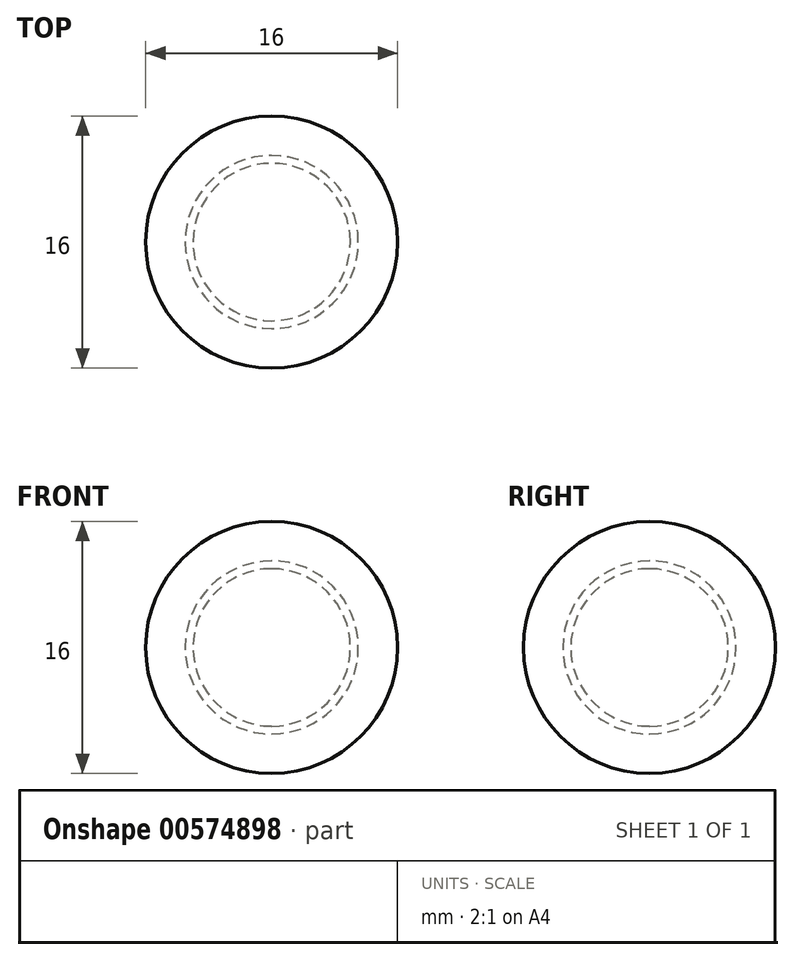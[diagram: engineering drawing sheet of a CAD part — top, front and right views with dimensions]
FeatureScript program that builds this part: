
annotation { "Feature Type Name" : "Feature", "Feature Type Description" : "" }
export const myFeature = defineFeature(function(context is Context, id is Id, definition is map)
    precondition{}
    {
        {
            var Q0;
            Q0=qCreatedBy(makeId("Right.planeOp"),FACE);
            var sketch = newSketch(context, id + "F0", { "sketchPlane" : qUnion([Q0])});
            skLineSegment(sketch, "E0", {"start": v(0, -5) * mm, "end": v(0, 5) * mm});
            skArc(sketch, "E1", {"start": v(0, -5) * mm, "mid": v(5, 0) * mm, "end": v(0, 5) * mm});
            skArc(sketch, "E2.0", {"start": v(0, -8) * mm, "mid": v(8, 0) * mm, "end": v(0, 8) * mm});
            skLineSegment(sketch, "E3", {"start": v(0, 5) * mm, "end": v(0, 8) * mm});
            skLineSegment(sketch, "E4", {"start": v(0, -5) * mm, "end": v(0, -8) * mm});
            skArc(sketch, "E5.0", {"start": v(0, -5.5) * mm, "mid": v(5.5, 0) * mm, "end": v(0, 5.5) * mm});
            skSolve(sketch);
        }
        {
            var Q0;
            Q0=makeQuery(id+"F0.imprint","IMPRINT",FACE,{"disambiguationData":[TD([[makeQuery(id+"F0.imprint","IMPRINT",EDGE,{"derivedFrom":sQuery(id+"F0.wireOp",EDGE,"E0")}),-1.0]])]});
            var Q1;
            Q1=sQuery(id+"F0.wireOp",EDGE,"E0");
            revolve(context, id + "F1", {"entities" : qUnion([Q0]), "axis" : qUnion([Q1]), "revolveType" : RevolveType.FULL});
        }
        {
            var Q0;
            {var subQ0=sQuery(id+"F0.wireOp",EDGE,"E2.0");Q0=makeQuery(id+"F0.imprint","IMPRINT",FACE,{"disambiguationData":[TD([[makeQuery(id+"F0.imprint","IMPRINT",EDGE,{"derivedFrom":subQ0}),1.0]])]});}
            var Q1;
            Q1=sQuery(id+"F0.wireOp",EDGE,"E3");
            revolve(context, id + "F2", {"entities" : qUnion([Q0]), "axis" : qUnion([Q1]), "revolveType" : RevolveType.FULL});
        }
    });
